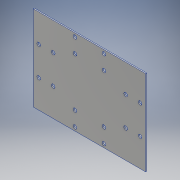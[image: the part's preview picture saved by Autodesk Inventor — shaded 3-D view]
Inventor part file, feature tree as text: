
AUTODESK INVENTOR PART (.ipt)
format: ipt  version: 2018.1 (Build 221171000, 171)  size: 133,632 bytes
history: native  units: mm
features: extrude x2, sketch x2, other x1
ambient origin geometry x8: Origin, YZ Plane, XZ Plane, XY Plane, X Axis, Y Axis, Z Axis, Center Point
bodies: Body1 (feature_tree)
feature tree (5):
  other  "ソリッド1"
  extrude  "押し出し1"  Depth=310.0mm
  extrude  "押し出し2"  Depth=235.0mm
  sketch  "スケッチ1"
  sketch  "スケッチ2"
